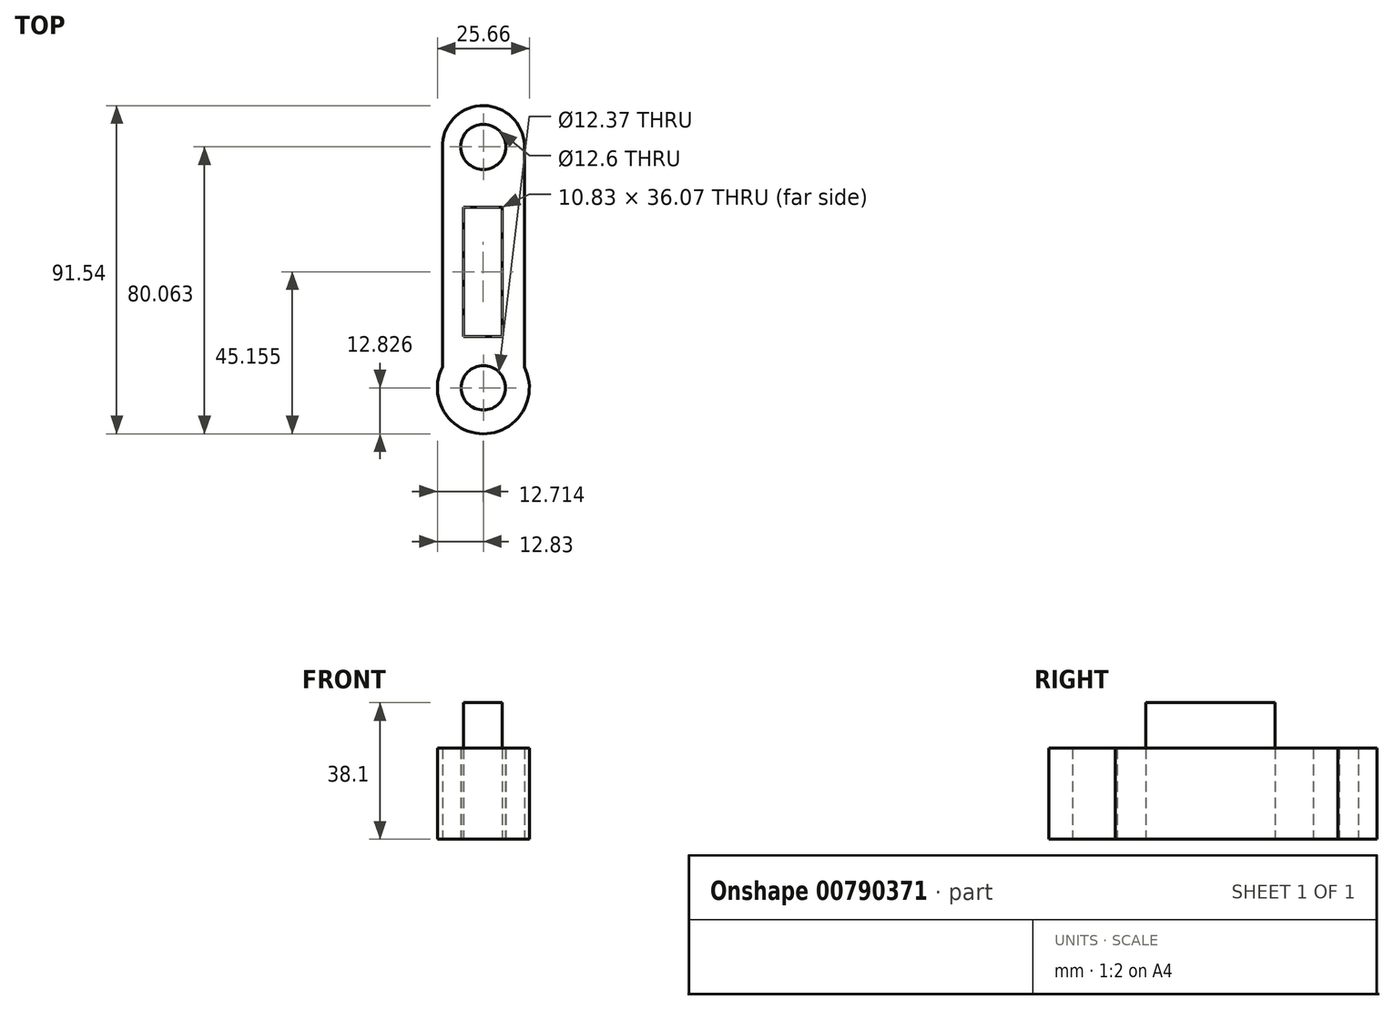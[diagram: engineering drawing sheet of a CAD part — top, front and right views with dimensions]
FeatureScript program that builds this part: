
annotation { "Feature Type Name" : "Feature", "Feature Type Description" : "" }
export const myFeature = defineFeature(function(context is Context, id is Id, definition is map)
    precondition{}
    {
        {
            var Q0;
            Q0=qCreatedBy(makeId("Top.planeOp"),FACE);
            var sketch = newSketch(context, id + "F0", { "sketchPlane" : qUnion([Q0])});
            skArc(sketch, "E0", {"start": v(11.45, 46.21) * mm, "mid": v(-0.15, 58.34) * mm, "end": v(-11.43, 45.9) * mm});
            skLineSegment(sketch, "E1", {"start": v(-11.43, 47.84) * mm, "end": v(-11.43, -14.58) * mm});
            skLineSegment(sketch, "E2", {"start": v(11.45, 47.54) * mm, "end": v(11.45, -14.58) * mm});
            skArc(sketch, "E3", {"start": v(-11.43, -14.54) * mm, "mid": v(-0.02, -33.2) * mm, "end": v(11.45, -14.58) * mm});
            skLineSegment(sketch, "E4", {"start": v(0.15, 58.34) * mm, "end": v(0, 46.87) * mm});
            skPoint(sketch, "E4.startSnap0", {"position": v(-0.15, 58.34) * mm});
            skLineSegment(sketch, "E5", {"start": v(0, 46.87) * mm, "end": v(0, -33.2) * mm});
            skCircle(sketch, "E6", {"center": v(0, -20.36) * mm, "radius": 6.19 * mm});
            skCircle(sketch, "E7", {"center": v(0, 46.87) * mm, "radius": 6.3 * mm});
            skLineSegment(sketch, "E8.bottom", {"start": v(5.3, -6.07) * mm, "end": v(-5.53, -6.07) * mm});
            skLineSegment(sketch, "E8.top", {"start": v(5.3, 30) * mm, "end": v(-5.53, 30) * mm});
            skLineSegment(sketch, "E8.left", {"start": v(5.3, -6.07) * mm, "end": v(5.3, 30) * mm});
            skLineSegment(sketch, "E8.right", {"start": v(-5.53, -6.07) * mm, "end": v(-5.53, 30) * mm});
            skSolve(sketch);
        }
        {
            var Q0;
            {var subQ16=sQuery(id+"F0.wireOp",EDGE,"E8.left");Q0=makeQuery(id+"F0.imprint","IMPRINT",FACE,{"disambiguationData":[TD([[makeQuery(id+"F0.imprint","IMPRINT",EDGE,{"derivedFrom":subQ16}),-1.0]])]});}
            var Q1;
            {var subQ16=sQuery(id+"F0.wireOp",EDGE,"E8.right");Q1=makeQuery(id+"F0.imprint","IMPRINT",FACE,{"disambiguationData":[TD([[makeQuery(id+"F0.imprint","IMPRINT",EDGE,{"derivedFrom":subQ16}),1.0]])]});}
            extrude(context, id + "F1", {"entities" : qUnion([Q0, Q1]), "depth" : 25.4 * mm, "offsetDistance" : 25.4 * mm});
        }
        {
            var Q0;
            Q0=makeQuery(id+"F1.opExtrude","CAP_FACE",FACE,{"disambiguationData":[OSD([sQuery(id+"F0.wireOp",EDGE,"E0"),sQuery(id+"F0.wireOp",EDGE,"E1"),sQuery(id+"F0.wireOp",EDGE,"E2"),sQuery(id+"F0.wireOp",EDGE,"E3"),sQuery(id+"F0.wireOp",EDGE,"E6"),sQuery(id+"F0.wireOp",EDGE,"E7"),sQuery(id+"F0.wireOp",EDGE,"E8.bottom"),sQuery(id+"F0.wireOp",EDGE,"E8.top"),sQuery(id+"F0.wireOp",EDGE,"E8.left"),sQuery(id+"F0.wireOp",EDGE,"E8.right")])],"isStart":false});
            var sketch = newSketch(context, id + "F2", { "sketchPlane" : qUnion([Q0])});
            skLineSegment(sketch, "E9.bottom", {"start": v(-5.53, -6.07) * mm, "end": v(5.3, -6.07) * mm});
            skLineSegment(sketch, "E9.top", {"start": v(-5.53, 30) * mm, "end": v(5.3, 30) * mm});
            skLineSegment(sketch, "E9.left", {"start": v(-5.53, -6.07) * mm, "end": v(-5.53, 30) * mm});
            skLineSegment(sketch, "E9.right", {"start": v(5.3, -6.07) * mm, "end": v(5.3, 30) * mm});
            skSolve(sketch);
        }
        {
            var Q0;
            Q0 = qSketchRegion(id + "F2", true);
            extrude(context, id + "F3", {"entities" : qUnion([Q0]), "depth" : 12.7 * mm, "offsetDistance" : 25.4 * mm});
        }
    });
